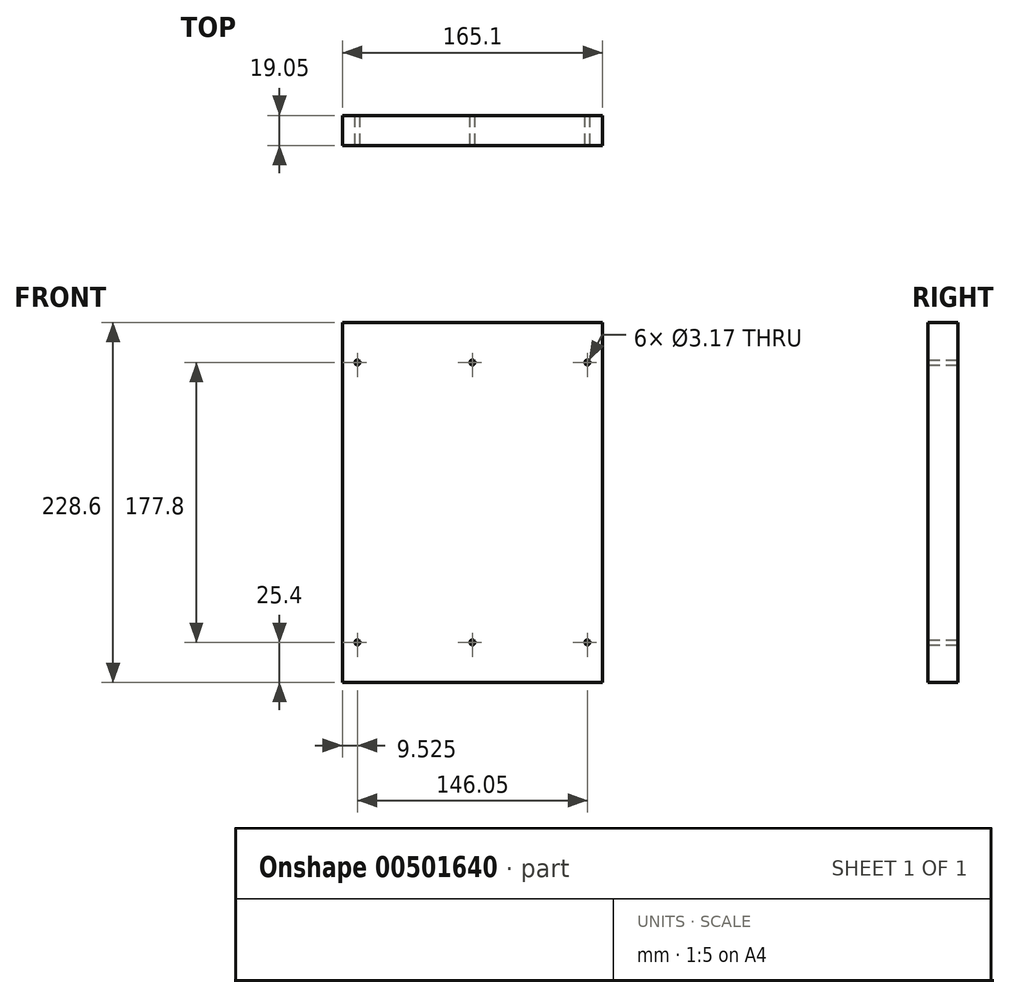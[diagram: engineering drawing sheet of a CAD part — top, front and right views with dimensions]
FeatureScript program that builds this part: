
annotation { "Feature Type Name" : "Feature", "Feature Type Description" : "" }
export const myFeature = defineFeature(function(context is Context, id is Id, definition is map)
    precondition{}
    {
        {
            var Q0;
            Q0=qCreatedBy(makeId("Front.planeOp"),FACE);
            var sketch = newSketch(context, id + "F0", { "sketchPlane" : qUnion([Q0])});
            skLineSegment(sketch, "E0.bottom", {"start": v(82.55, 114.3) * mm, "end": v(-82.55, 114.3) * mm});
            skLineSegment(sketch, "E0.top", {"start": v(82.55, -114.3) * mm, "end": v(-82.55, -114.3) * mm});
            skLineSegment(sketch, "E0.left", {"start": v(82.55, 114.3) * mm, "end": v(82.55, -114.3) * mm});
            skLineSegment(sketch, "E0.right", {"start": v(-82.55, 114.3) * mm, "end": v(-82.55, -114.3) * mm});
            skPoint(sketch, "E0.middle", {"position": v(0, 0) * mm});
            skLineSegment(sketch, "E1", {"start": v(0, -114.3) * mm, "end": v(0, 114.3) * mm, "construction": true});
            skCircle(sketch, "E2", {"center": v(73.03, 88.9) * mm, "radius": 1.59 * mm});
            skLineSegment(sketch, "E3", {"start": v(73.02, 114.3) * mm, "end": v(73.03, -114.3) * mm, "construction": true});
            skLineSegment(sketch, "E4", {"start": v(0, 0) * mm, "end": v(82.55, 0) * mm, "construction": true});
            skCircle(sketch, "E5", {"center": v(0, 88.9) * mm, "radius": 1.59 * mm});
            skCircle(sketch, "E6.MirrorC", {"center": v(0, -88.9) * mm, "radius": 1.59 * mm});
            skCircle(sketch, "E7.MirrorC", {"center": v(73.03, -88.9) * mm, "radius": 1.59 * mm});
            skCircle(sketch, "E8.MirrorC", {"center": v(-73.02, -88.9) * mm, "radius": 1.59 * mm});
            skCircle(sketch, "E9.MirrorC", {"center": v(-73.02, 88.9) * mm, "radius": 1.59 * mm});
            skLineSegment(sketch, "E10.MirrorCS", {"start": v(0, 0) * mm, "end": v(-82.55, 0) * mm, "construction": true});
            skSolve(sketch);
        }
        {
            var Q0;
            Q0=qSketchRegion(id+"F0",true);
            extrude(context, id + "F1", {"entities" : qUnion([Q0]), "depth" : 19.05 * mm});
        }
    });
